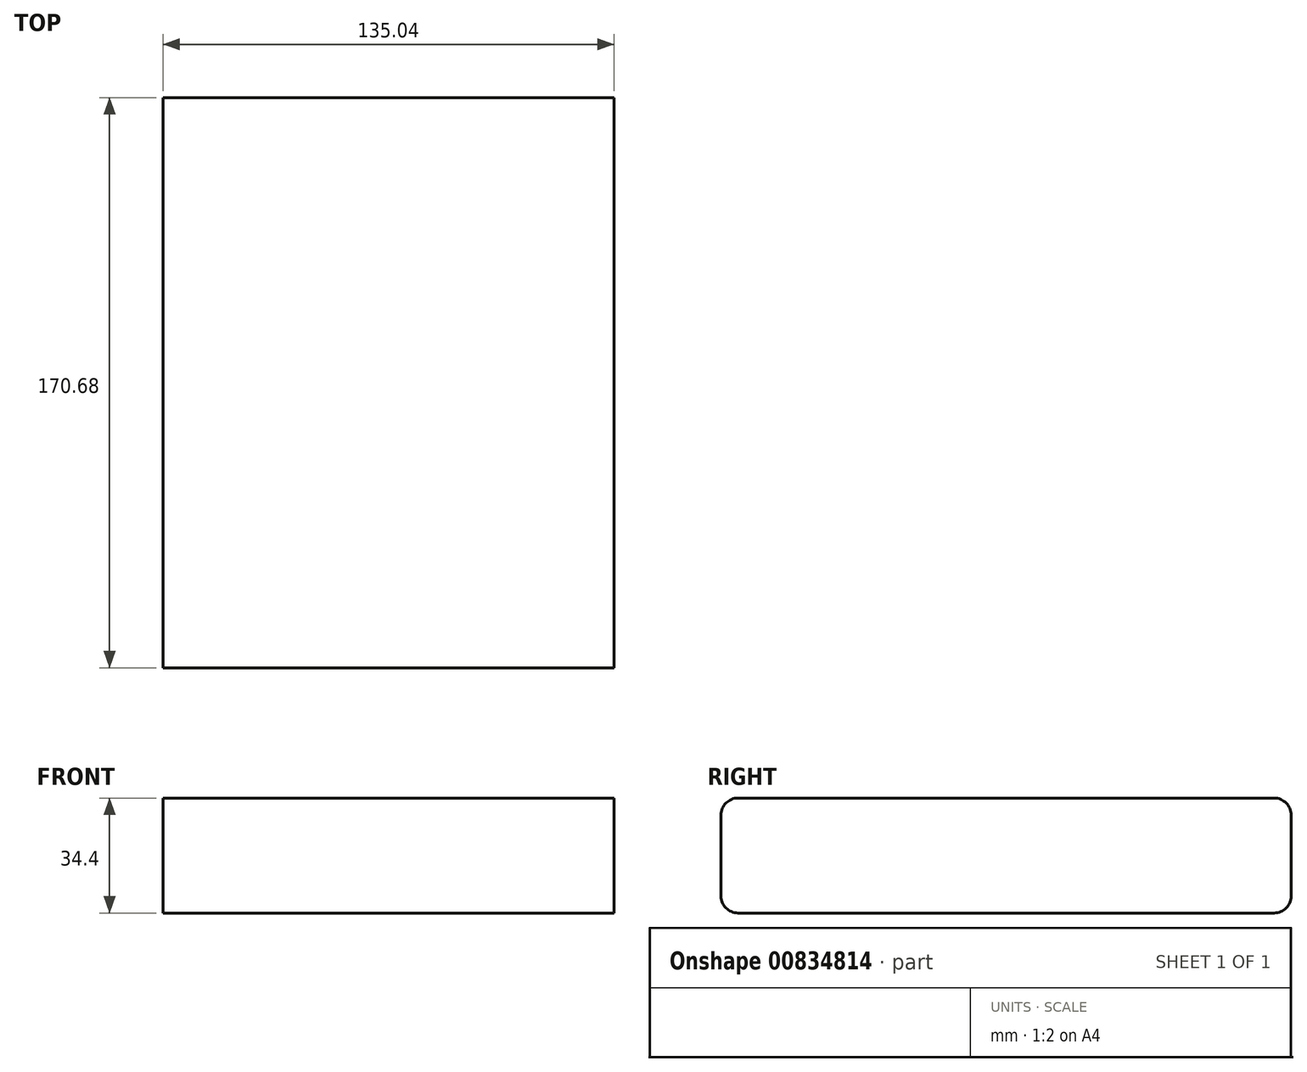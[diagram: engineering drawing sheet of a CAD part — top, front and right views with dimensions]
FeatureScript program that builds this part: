
annotation { "Feature Type Name" : "Feature", "Feature Type Description" : "" }
export const myFeature = defineFeature(function(context is Context, id is Id, definition is map)
    precondition{}
    {
        {
            var Q0;
            Q0=qCreatedBy(makeId("Front.planeOp"),FACE);
            var sketch = newSketch(context, id + "F0", { "sketchPlane" : qUnion([Q0])});
            skLineSegment(sketch, "E0.bottom", {"start": v(67.52, -17.2) * mm, "end": v(-67.52, -17.2) * mm});
            skLineSegment(sketch, "E0.top", {"start": v(67.52, 17.2) * mm, "end": v(-67.52, 17.2) * mm});
            skLineSegment(sketch, "E0.left", {"start": v(67.52, -17.2) * mm, "end": v(67.52, 17.2) * mm});
            skLineSegment(sketch, "E0.right", {"start": v(-67.52, -17.2) * mm, "end": v(-67.52, 17.2) * mm});
            skPoint(sketch, "E0.middle", {"position": v(0, 0) * mm});
            skSolve(sketch);
        }
        {
            var Q0;
            Q0=makeQuery(id+"F0.imprint","IMPRINT",FACE,{"disambiguationData":[TD([[makeQuery(id+"F0.imprint","IMPRINT",EDGE,{"derivedFrom":sQuery(id+"F0.wireOp",EDGE,"E0.bottom")}),-1.0]])]});
            extrude(context, id + "F1", {"entities" : qUnion([Q0]), "endBound" : BoundingType.SYMMETRIC, "depth" : 170.7 * mm, "offsetDistance" : 25.4 * mm});
        }
        {
            var Q0;
            Q0=makeQuery(id+"F1.opExtrude","CAP_EDGE",EDGE,{"disambiguationData":[OSD([sQuery(id+"F0.wireOp",EDGE,"E0.top")])],"isStart":false});
            var Q1;
            Q1=makeQuery(id+"F1.opExtrude","CAP_EDGE",EDGE,{"disambiguationData":[OSD([sQuery(id+"F0.wireOp",EDGE,"E0.top")])],"isStart":true});
            var Q2;
            Q2=makeQuery(id+"F1.opExtrude","CAP_EDGE",EDGE,{"disambiguationData":[OSD([sQuery(id+"F0.wireOp",EDGE,"E0.bottom")])],"isStart":false});
            var Q3;
            Q3=makeQuery(id+"F1.opExtrude","CAP_EDGE",EDGE,{"disambiguationData":[OSD([sQuery(id+"F0.wireOp",EDGE,"E0.bottom")])],"isStart":true});
            fillet(context, id + "F2", {"entities" : qUnion([Q0, Q1, Q2, Q3]), "radius" : 5.08 * mm, "tangentPropagation" : true, "allowEdgeOverflow" : false});
        }
    });
